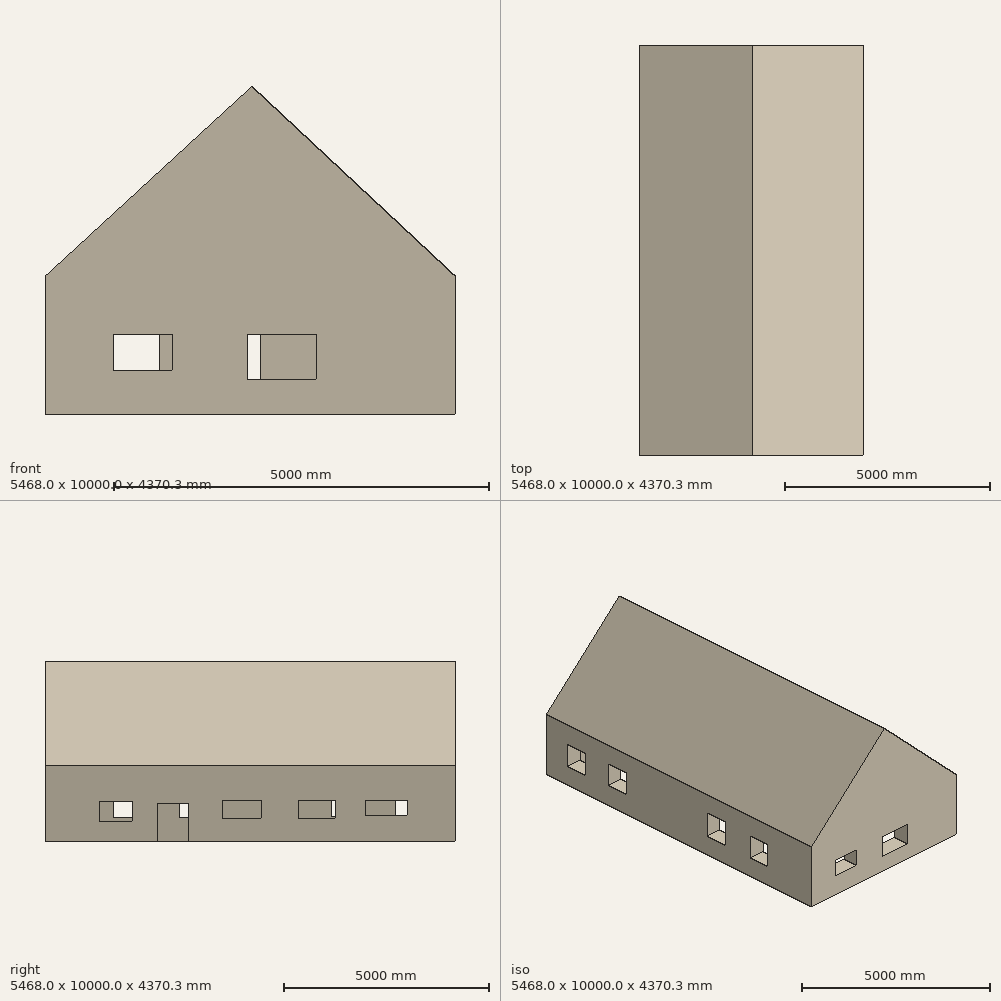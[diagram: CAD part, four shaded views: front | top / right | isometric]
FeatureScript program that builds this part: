
annotation { "Feature Type Name" : "Feature", "Feature Type Description" : "" }
export const myFeature = defineFeature(function(context is Context, id is Id, definition is map)
    precondition{}
    {
        {
            var Q0;
            Q0=qCreatedBy(makeId("Top.planeOp"),FACE);
            var sketch = newSketch(context, id + "F0", { "sketchPlane" : qUnion([Q0])});
            skLineSegment(sketch, "E0.bottom", {"start": v(0, 0) * mm, "end": v(-5468, 0) * mm});
            skLineSegment(sketch, "E0.top", {"start": v(0, 10000) * mm, "end": v(-5468, 10000) * mm});
            skLineSegment(sketch, "E0.left", {"start": v(0, 0) * mm, "end": v(0, 10000) * mm});
            skLineSegment(sketch, "E0.right", {"start": v(-5468, 0) * mm, "end": v(-5468, 10000) * mm});
            skLineSegment(sketch, "E1.bottom", {"start": v(-4989.22, 9378.49) * mm, "end": v(-500.42, 9378.49) * mm});
            skLineSegment(sketch, "E1.top", {"start": v(-4989.22, 475.42) * mm, "end": v(-500.42, 475.42) * mm});
            skLineSegment(sketch, "E1.left", {"start": v(-4989.22, 9378.49) * mm, "end": v(-4989.22, 475.42) * mm});
            skLineSegment(sketch, "E1.right", {"start": v(-500.42, 9378.49) * mm, "end": v(-500.42, 475.42) * mm});
            skSolve(sketch);
        }
        {
            var Q0;
            {var subQ7=sQuery(id+"F0.wireOp",EDGE,"E0.bottom");Q0=makeQuery(id+"F0.imprint","IMPRINT",FACE,{"disambiguationData":[TD([[makeQuery(id+"F0.imprint","IMPRINT",EDGE,{"derivedFrom":subQ7}),-1.0]])]});}
            extrude(context, id + "F1", {"entities" : qUnion([Q0]), "depth" : 1840 * mm, "offsetDistance" : 25 * mm});
        }
        {
            var Q0;
            Q0=makeQuery(id+"F1.opExtrude","SWEPT_FACE",FACE,{"disambiguationData":[OSD([sQuery(id+"F0.wireOp",EDGE,"E0.left")])]});
            var sketch = newSketch(context, id + "F2", { "sketchPlane" : qUnion([Q0])});
            skLineSegment(sketch, "E2.bottom", {"start": v(2741.88, 922.3) * mm, "end": v(3487.98, 922.3) * mm});
            skLineSegment(sketch, "E2.top", {"start": v(2741.88, 0) * mm, "end": v(3487.98, 0) * mm});
            skLineSegment(sketch, "E2.left", {"start": v(2741.88, 922.3) * mm, "end": v(2741.88, 0) * mm});
            skLineSegment(sketch, "E2.right", {"start": v(3487.98, 922.3) * mm, "end": v(3487.98, 0) * mm});
            skLineSegment(sketch, "E3.bottom", {"start": v(4307.27, 989.85) * mm, "end": v(5257.06, 989.85) * mm});
            skLineSegment(sketch, "E3.top", {"start": v(4307.27, 542.31) * mm, "end": v(5257.06, 542.31) * mm});
            skLineSegment(sketch, "E3.left", {"start": v(4307.27, 989.85) * mm, "end": v(4307.27, 542.31) * mm});
            skLineSegment(sketch, "E3.right", {"start": v(5257.06, 989.85) * mm, "end": v(5257.06, 542.31) * mm});
            skLineSegment(sketch, "E4.bottom", {"start": v(6159.15, 1001.61) * mm, "end": v(7065.2, 1001.61) * mm});
            skLineSegment(sketch, "E4.top", {"start": v(6159.15, 544.46) * mm, "end": v(7065.2, 544.46) * mm});
            skLineSegment(sketch, "E4.left", {"start": v(6159.15, 1001.61) * mm, "end": v(6159.15, 544.46) * mm});
            skLineSegment(sketch, "E4.right", {"start": v(7065.2, 1001.61) * mm, "end": v(7065.2, 544.46) * mm});
            skLineSegment(sketch, "E5.bottom", {"start": v(7802.9, 980.44) * mm, "end": v(8831.37, 980.44) * mm});
            skLineSegment(sketch, "E5.top", {"start": v(7802.9, 613) * mm, "end": v(8831.37, 613) * mm});
            skLineSegment(sketch, "E5.left", {"start": v(7802.9, 980.44) * mm, "end": v(7802.9, 613) * mm});
            skLineSegment(sketch, "E5.right", {"start": v(8831.37, 980.44) * mm, "end": v(8831.37, 613) * mm});
            skLineSegment(sketch, "E6.bottom", {"start": v(1316.35, 965.52) * mm, "end": v(2124.4, 965.52) * mm});
            skLineSegment(sketch, "E6.top", {"start": v(1316.35, 473.91) * mm, "end": v(2124.4, 473.91) * mm});
            skLineSegment(sketch, "E6.left", {"start": v(1316.35, 965.52) * mm, "end": v(1316.35, 473.91) * mm});
            skLineSegment(sketch, "E6.right", {"start": v(2124.4, 965.52) * mm, "end": v(2124.4, 473.91) * mm});
            skSolve(sketch);
        }
        {
            var Q0;
            Q0=makeQuery(id+"F2.imprint","IMPRINT",FACE,{"disambiguationData":[TD([[makeQuery(id+"F2.imprint","IMPRINT",EDGE,{"derivedFrom":sQuery(id+"F2.wireOp",EDGE,"E2.bottom")}),-1.0]])]});
            var Q1;
            Q1=makeQuery(id+"F2.imprint","IMPRINT",FACE,{"disambiguationData":[TD([[makeQuery(id+"F2.imprint","IMPRINT",EDGE,{"derivedFrom":sQuery(id+"F2.wireOp",EDGE,"E6.bottom")}),-1.0]])]});
            var Q2;
            Q2=makeQuery(id+"F2.imprint","IMPRINT",FACE,{"disambiguationData":[TD([[makeQuery(id+"F2.imprint","IMPRINT",EDGE,{"derivedFrom":sQuery(id+"F2.wireOp",EDGE,"E3.bottom")}),-1.0]])]});
            var Q3;
            Q3=makeQuery(id+"F2.imprint","IMPRINT",FACE,{"disambiguationData":[TD([[makeQuery(id+"F2.imprint","IMPRINT",EDGE,{"derivedFrom":sQuery(id+"F2.wireOp",EDGE,"E4.bottom")}),-1.0]])]});
            var Q4;
            Q4=makeQuery(id+"F2.imprint","IMPRINT",FACE,{"disambiguationData":[TD([[makeQuery(id+"F2.imprint","IMPRINT",EDGE,{"derivedFrom":sQuery(id+"F2.wireOp",EDGE,"E5.bottom")}),-1.0]])]});
            extrude(context, id + "F3", {"entities" : qUnion([Q0, Q1, Q2, Q3, Q4]), "operationType" : NewBodyOperationType.REMOVE, "endBound" : BoundingType.UP_TO_NEXT, "oppositeDirection" : true, "depth" : 570 * mm, "offsetDistance" : 25 * mm});
        }
        {
            var Q0;
            Q0=makeQuery(id+"F1.opExtrude","SWEPT_FACE",FACE,{"disambiguationData":[OSD([sQuery(id+"F0.wireOp",EDGE,"E0.bottom")])]});
            var sketch = newSketch(context, id + "F4", { "sketchPlane" : qUnion([Q0])});
            skLineSegment(sketch, "E7.bottom", {"start": v(-4561.06, 1059.2) * mm, "end": v(-3767.61, 1059.2) * mm});
            skLineSegment(sketch, "E7.top", {"start": v(-4561.06, 588.54) * mm, "end": v(-3767.61, 588.54) * mm});
            skLineSegment(sketch, "E7.left", {"start": v(-4561.06, 1059.2) * mm, "end": v(-4561.06, 588.54) * mm});
            skLineSegment(sketch, "E7.right", {"start": v(-3767.61, 1059.2) * mm, "end": v(-3767.61, 588.54) * mm});
            skLineSegment(sketch, "E8.bottom", {"start": v(-2778.97, 1061.96) * mm, "end": v(-1850.11, 1061.96) * mm});
            skLineSegment(sketch, "E8.top", {"start": v(-2778.97, 468.76) * mm, "end": v(-1850.11, 468.76) * mm});
            skLineSegment(sketch, "E8.left", {"start": v(-2778.97, 1061.96) * mm, "end": v(-2778.97, 468.76) * mm});
            skLineSegment(sketch, "E8.right", {"start": v(-1850.11, 1061.96) * mm, "end": v(-1850.11, 468.76) * mm});
            skLineSegment(sketch, "E9", {"start": v(-5468, 1840) * mm, "end": v(-2712.48, 4370.3) * mm});
            skLineSegment(sketch, "E10", {"start": v(-2712.48, 4370.3) * mm, "end": v(0, 1840) * mm});
            skLineSegment(sketch, "E11", {"start": v(0, 1840) * mm, "end": v(-5468, 1840) * mm});
            skSolve(sketch);
        }
        {
            var Q0;
            Q0=makeQuery(id+"F4.imprint","IMPRINT",FACE,{"disambiguationData":[TD([[makeQuery(id+"F4.imprint","IMPRINT",EDGE,{"derivedFrom":sQuery(id+"F4.wireOp",EDGE,"E7.bottom")}),-1.0]])]});
            var Q1;
            Q1=makeQuery(id+"F4.imprint","IMPRINT",FACE,{"disambiguationData":[TD([[makeQuery(id+"F4.imprint","IMPRINT",EDGE,{"derivedFrom":sQuery(id+"F4.wireOp",EDGE,"E8.bottom")}),-1.0]])]});
            extrude(context, id + "F5", {"entities" : qUnion([Q0, Q1]), "operationType" : NewBodyOperationType.REMOVE, "endBound" : BoundingType.UP_TO_NEXT, "oppositeDirection" : true, "depth" : 25 * mm, "offsetDistance" : 25 * mm});
        }
        {
            var Q0;
            Q0=makeQuery(id+"F1.opExtrude","SWEPT_FACE",FACE,{"disambiguationData":[OSD([sQuery(id+"F0.wireOp",EDGE,"E0.top")])]});
            var sketch = newSketch(context, id + "F6", { "sketchPlane" : qUnion([Q0])});
            skLineSegment(sketch, "E12.bottom", {"start": v(1014.6, 1126.72) * mm, "end": v(1697.35, 1126.72) * mm});
            skLineSegment(sketch, "E12.top", {"start": v(1014.6, 422.48) * mm, "end": v(1697.35, 422.48) * mm});
            skLineSegment(sketch, "E12.left", {"start": v(1014.6, 1126.72) * mm, "end": v(1014.6, 422.48) * mm});
            skLineSegment(sketch, "E12.right", {"start": v(1697.35, 1126.72) * mm, "end": v(1697.35, 422.48) * mm});
            skLineSegment(sketch, "E13.bottom", {"start": v(2605.26, 1118.65) * mm, "end": v(3283.35, 1118.65) * mm});
            skLineSegment(sketch, "E13.top", {"start": v(2605.26, 361.4) * mm, "end": v(3283.35, 361.4) * mm});
            skLineSegment(sketch, "E13.left", {"start": v(2605.26, 1118.65) * mm, "end": v(2605.26, 361.4) * mm});
            skLineSegment(sketch, "E13.right", {"start": v(3283.35, 1118.65) * mm, "end": v(3283.35, 361.4) * mm});
            skLineSegment(sketch, "E14.bottom", {"start": v(3942.5, 1059.24) * mm, "end": v(4583.19, 1059.24) * mm});
            skLineSegment(sketch, "E14.top", {"start": v(3942.5, 361.4) * mm, "end": v(4583.19, 361.4) * mm});
            skLineSegment(sketch, "E14.left", {"start": v(3942.5, 1059.24) * mm, "end": v(3942.5, 361.4) * mm});
            skLineSegment(sketch, "E14.right", {"start": v(4583.19, 1059.24) * mm, "end": v(4583.19, 361.4) * mm});
            skSolve(sketch);
        }
        {
            var Q0;
            Q0=makeQuery(id+"F6.imprint","IMPRINT",FACE,{"disambiguationData":[TD([[makeQuery(id+"F6.imprint","IMPRINT",EDGE,{"derivedFrom":sQuery(id+"F6.wireOp",EDGE,"E12.bottom")}),-1.0]])]});
            var Q1;
            Q1=makeQuery(id+"F6.imprint","IMPRINT",FACE,{"disambiguationData":[TD([[makeQuery(id+"F6.imprint","IMPRINT",EDGE,{"derivedFrom":sQuery(id+"F6.wireOp",EDGE,"E13.bottom")}),-1.0]])]});
            var Q2;
            Q2=makeQuery(id+"F6.imprint","IMPRINT",FACE,{"disambiguationData":[TD([[makeQuery(id+"F6.imprint","IMPRINT",EDGE,{"derivedFrom":sQuery(id+"F6.wireOp",EDGE,"E14.bottom")}),-1.0]])]});
            extrude(context, id + "F7", {"entities" : qUnion([Q0, Q1, Q2]), "operationType" : NewBodyOperationType.REMOVE, "endBound" : BoundingType.UP_TO_NEXT, "oppositeDirection" : true, "depth" : 25 * mm, "offsetDistance" : 25 * mm});
        }
        {
            var Q0;
            Q0=makeQuery(id+"F1.opExtrude","SWEPT_FACE",FACE,{"disambiguationData":[OSD([sQuery(id+"F0.wireOp",EDGE,"E0.right")])]});
            var sketch = newSketch(context, id + "F8", { "sketchPlane" : qUnion([Q0])});
            skLineSegment(sketch, "E15.bottom", {"start": v(-9210.07, 1248.14) * mm, "end": v(-8540.1, 1248.14) * mm});
            skLineSegment(sketch, "E15.top", {"start": v(-9210.07, 567.59) * mm, "end": v(-8540.1, 567.59) * mm});
            skLineSegment(sketch, "E15.left", {"start": v(-9210.07, 1248.14) * mm, "end": v(-9210.07, 567.59) * mm});
            skLineSegment(sketch, "E15.right", {"start": v(-8540.1, 1248.14) * mm, "end": v(-8540.1, 567.59) * mm});
            skLineSegment(sketch, "E16.bottom", {"start": v(-7674.81, 1280.79) * mm, "end": v(-6980.7, 1280.79) * mm});
            skLineSegment(sketch, "E16.top", {"start": v(-7674.81, 609.69) * mm, "end": v(-6980.7, 609.69) * mm});
            skLineSegment(sketch, "E16.left", {"start": v(-7674.81, 1280.79) * mm, "end": v(-7674.81, 609.69) * mm});
            skLineSegment(sketch, "E16.right", {"start": v(-6980.7, 1280.79) * mm, "end": v(-6980.7, 609.69) * mm});
            skLineSegment(sketch, "E17.bottom", {"start": v(-3944.72, 1285.43) * mm, "end": v(-3259.56, 1285.43) * mm});
            skLineSegment(sketch, "E17.top", {"start": v(-3944.72, 569.23) * mm, "end": v(-3259.56, 569.23) * mm});
            skLineSegment(sketch, "E17.left", {"start": v(-3944.72, 1285.43) * mm, "end": v(-3944.72, 569.23) * mm});
            skLineSegment(sketch, "E17.right", {"start": v(-3259.56, 1285.43) * mm, "end": v(-3259.56, 569.23) * mm});
            skLineSegment(sketch, "E18.bottom", {"start": v(-2308.62, 1246.64) * mm, "end": v(-1667.85, 1246.64) * mm});
            skLineSegment(sketch, "E18.top", {"start": v(-2308.62, 568.52) * mm, "end": v(-1667.85, 568.52) * mm});
            skLineSegment(sketch, "E18.left", {"start": v(-2308.62, 1246.64) * mm, "end": v(-2308.62, 568.52) * mm});
            skLineSegment(sketch, "E18.right", {"start": v(-1667.85, 1246.64) * mm, "end": v(-1667.85, 568.52) * mm});
            skSolve(sketch);
        }
        {
            var Q0;
            Q0=makeQuery(id+"F8.imprint","IMPRINT",FACE,{"disambiguationData":[TD([[makeQuery(id+"F8.imprint","IMPRINT",EDGE,{"derivedFrom":sQuery(id+"F8.wireOp",EDGE,"E15.bottom")}),-1.0]])]});
            var Q1;
            Q1=makeQuery(id+"F8.imprint","IMPRINT",FACE,{"disambiguationData":[TD([[makeQuery(id+"F8.imprint","IMPRINT",EDGE,{"derivedFrom":sQuery(id+"F8.wireOp",EDGE,"E16.bottom")}),-1.0]])]});
            var Q2;
            Q2=makeQuery(id+"F8.imprint","IMPRINT",FACE,{"disambiguationData":[TD([[makeQuery(id+"F8.imprint","IMPRINT",EDGE,{"derivedFrom":sQuery(id+"F8.wireOp",EDGE,"E17.bottom")}),-1.0]])]});
            var Q3;
            Q3=makeQuery(id+"F8.imprint","IMPRINT",FACE,{"disambiguationData":[TD([[makeQuery(id+"F8.imprint","IMPRINT",EDGE,{"derivedFrom":sQuery(id+"F8.wireOp",EDGE,"E18.bottom")}),-1.0]])]});
            extrude(context, id + "F9", {"entities" : qUnion([Q0, Q1, Q2, Q3]), "operationType" : NewBodyOperationType.REMOVE, "endBound" : BoundingType.UP_TO_NEXT, "oppositeDirection" : true, "depth" : 25 * mm, "offsetDistance" : 25 * mm});
        }
        {
            var Q0;
            Q0=makeQuery(id+"F4.imprint","IMPRINT",FACE,{"disambiguationData":[TD([[makeQuery(id+"F4.imprint","IMPRINT",EDGE,{"derivedFrom":sQuery(id+"F4.wireOp",EDGE,"E9")}),-1.0]])]});
            extrude(context, id + "F10", {"entities" : qUnion([Q0]), "operationType" : NewBodyOperationType.ADD, "oppositeDirection" : true, "depth" : 10000 * mm, "offsetDistance" : 25 * mm});
        }
    });
